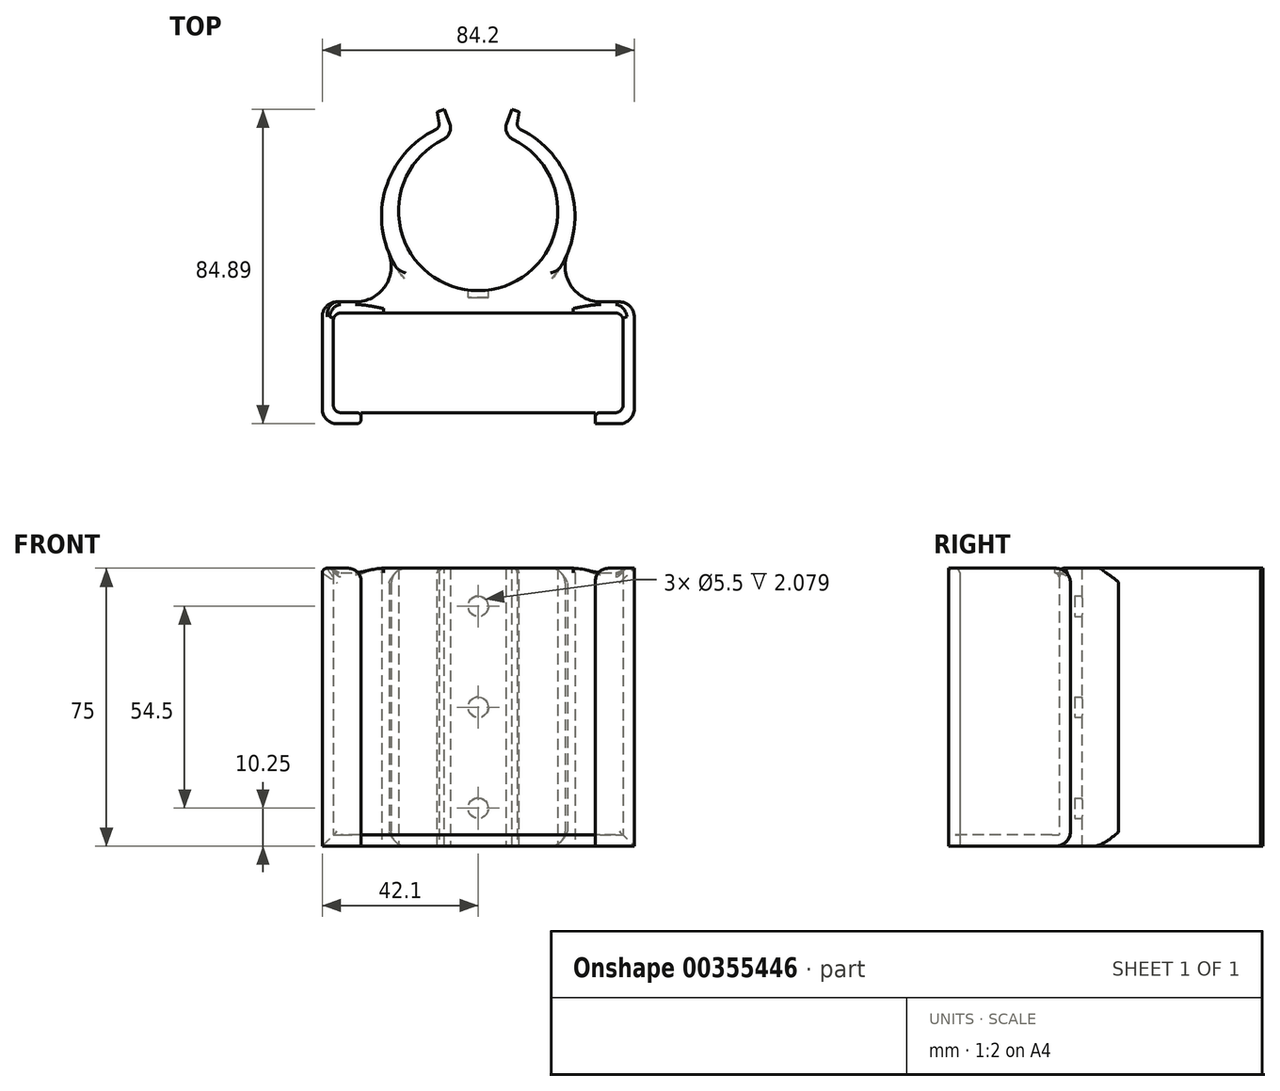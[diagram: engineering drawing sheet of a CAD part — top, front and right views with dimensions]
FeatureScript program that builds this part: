
annotation { "Feature Type Name" : "Feature", "Feature Type Description" : "" }
export const myFeature = defineFeature(function(context is Context, id is Id, definition is map)
    precondition{}
    {
        {
            var Q0;
            Q0=qCreatedBy(makeId("Top.planeOp"),FACE);
            var sketch = newSketch(context, id + "F0", { "sketchPlane" : qUnion([Q0])});
            skLineSegment(sketch, "E0", {"start": v(39.1, 0) * mm, "end": v(42.1, 0) * mm});
            skLineSegment(sketch, "E1", {"start": v(42.1, 0) * mm, "end": v(42.1, -3) * mm});
            skLineSegment(sketch, "E2", {"start": v(42.1, -3) * mm, "end": v(42.1, -29.9) * mm});
            skLineSegment(sketch, "E3", {"start": v(42.1, -29.9) * mm, "end": v(42.1, -32.9) * mm});
            skLineSegment(sketch, "E4", {"start": v(42.1, -32.9) * mm, "end": v(33.1, -32.9) * mm});
            skLineSegment(sketch, "E5", {"start": v(33.1, -29.9) * mm, "end": v(39.1, -29.9) * mm});
            skLineSegment(sketch, "E6", {"start": v(39.1, -29.9) * mm, "end": v(39.1, -3) * mm});
            skLineSegment(sketch, "E7", {"start": v(39.1, -3) * mm, "end": v(-39.1, -3) * mm});
            skLineSegment(sketch, "E8", {"start": v(-39.1, -3) * mm, "end": v(-39.1, -29.9) * mm});
            skLineSegment(sketch, "E9", {"start": v(-39.1, -29.9) * mm, "end": v(-33.1, -29.9) * mm});
            skLineSegment(sketch, "E10", {"start": v(-33.1, -32.9) * mm, "end": v(-42.1, -32.9) * mm});
            skLineSegment(sketch, "E11", {"start": v(-42.1, -32.9) * mm, "end": v(-42.1, 0) * mm});
            skLineSegment(sketch, "E12", {"start": v(-42.1, 0) * mm, "end": v(-33.1, 0) * mm});
            skArc(sketch, "E13", {"start": v(-33.1, 0) * mm, "mid": v(-25.18, 4.14) * mm, "end": v(-24.06, 13) * mm});
            skArc(sketch, "E14", {"start": v(24.06, 13) * mm, "mid": v(25.18, 4.14) * mm, "end": v(33.1, 0) * mm});
            skArc(sketch, "E15", {"start": v(-15.28, 44.25) * mm, "mid": v(-25.12, 30.16) * mm, "end": v(-24.06, 13) * mm});
            skArc(sketch, "E16", {"start": v(24.06, 13) * mm, "mid": v(25.12, 30.16) * mm, "end": v(15.28, 44.25) * mm});
            skLineSegment(sketch, "E17", {"start": v(33.1, 0) * mm, "end": v(39.1, 0) * mm});
            skLineSegment(sketch, "E18", {"start": v(-33.1, -32.9) * mm, "end": v(33.1, -32.9) * mm});
            skLineSegment(sketch, "E19", {"start": v(-33.1, -29.9) * mm, "end": v(33.1, -29.9) * mm});
            skLineSegment(sketch, "E20", {"start": v(-33.1, 0) * mm, "end": v(33.1, 0) * mm});
            skLineSegment(sketch, "E21", {"start": v(-42.1, -32.9) * mm, "end": v(-31.6, -32.9) * mm});
            skLineSegment(sketch, "E22", {"start": v(-31.6, -32.9) * mm, "end": v(-31.6, -29.9) * mm});
            skLineSegment(sketch, "E23", {"start": v(42.1, -32.9) * mm, "end": v(31.6, -32.9) * mm});
            skLineSegment(sketch, "E24", {"start": v(31.6, -32.9) * mm, "end": v(31.6, -29.9) * mm});
            skArc(sketch, "E25", {"start": v(-5.92, 45.2) * mm, "mid": v(0, 3.04) * mm, "end": v(5.9, 45.2) * mm});
            skLineSegment(sketch, "E26", {"start": v(5.9, 45.2) * mm, "end": v(9.5, 54.53) * mm});
            skLineSegment(sketch, "E27", {"start": v(-9.5, 54.53) * mm, "end": v(-5.92, 45.2) * mm});
            skLineSegment(sketch, "E28", {"start": v(9.5, 54.53) * mm, "end": v(11.36, 53.81) * mm});
            skLineSegment(sketch, "E29", {"start": v(-9.5, 54.53) * mm, "end": v(-11.37, 53.82) * mm});
            skLineSegment(sketch, "E30", {"start": v(-11.37, 53.82) * mm, "end": v(-10.43, 47.02) * mm});
            skPoint(sketch, "E30.endSnap0", {"position": v(-10.43, 54.17) * mm});
            skLineSegment(sketch, "E31", {"start": v(11.36, 53.81) * mm, "end": v(10.42, 47.02) * mm});
            skPoint(sketch, "E31.endSnap0", {"position": v(10.42, 54.17) * mm});
            skArc(sketch, "E32", {"start": v(-10.43, 47.02) * mm, "mid": v(-24.22, 32.8) * mm, "end": v(-24.06, 13) * mm});
            skArc(sketch, "E33", {"start": v(24.06, 13) * mm, "mid": v(24.22, 32.8) * mm, "end": v(10.42, 47.02) * mm});
            skSolve(sketch);
        }
        {
            var Q0;
            {var subQ1=sQuery(id+"F0.wireOp",EDGE,"E5");Q0=makeQuery(id+"F0.imprint","IMPRINT",FACE,{"disambiguationData":[TD([[makeQuery(id+"F0.imprint","IMPRINT",EDGE,{"derivedFrom":subQ1}),1.0]])]});}
            extrude(context, id + "F1", {"entities" : qUnion([Q0]), "depth" : 3 * mm});
        }
        {
            var Q0;
            Q0=makeQuery(id+"F0.imprint","IMPRINT",FACE,{"disambiguationData":[TD([[makeQuery(id+"F0.imprint","IMPRINT",EDGE,{"derivedFrom":sQuery(id+"F0.wireOp",EDGE,"E18")}),1.0]])]});
            extrude(context, id + "F2", {"entities" : qUnion([Q0]), "operationType" : NewBodyOperationType.ADD, "depth" : 8 * mm});
        }
        {
            var Q0;
            Q0=makeQuery(id+"F0.imprint","IMPRINT",FACE,{"disambiguationData":[TD([[makeQuery(id+"F0.imprint","IMPRINT",EDGE,{"derivedFrom":sQuery(id+"F0.wireOp",EDGE,"E0")}),-1.0]])]});
            var Q1;
            {var subQ1=sQuery(id+"F0.wireOp",EDGE,"E13");Q1=makeQuery(id+"F0.imprint","IMPRINT",FACE,{"disambiguationData":[TD([[makeQuery(id+"F0.imprint","IMPRINT",EDGE,{"derivedFrom":subQ1}),-1.0]])]});}
            extrude(context, id + "F3", {"entities" : qUnion([Q0, Q1]), "operationType" : NewBodyOperationType.ADD, "depth" : 75 * mm});
        }
        {
            var Q0;
            Q0=makeQuery(id+"F3.opExtrude","CAP_FACE",FACE,{"disambiguationData":[OSD([sQuery(id+"F0.wireOp",EDGE,"E0"),sQuery(id+"F0.wireOp",EDGE,"E1"),sQuery(id+"F0.wireOp",EDGE,"E2"),sQuery(id+"F0.wireOp",EDGE,"E3"),sQuery(id+"F0.wireOp",EDGE,"E5"),sQuery(id+"F0.wireOp",EDGE,"E6"),sQuery(id+"F0.wireOp",EDGE,"E7"),sQuery(id+"F0.wireOp",EDGE,"E8"),sQuery(id+"F0.wireOp",EDGE,"E9"),sQuery(id+"F0.wireOp",EDGE,"E11"),sQuery(id+"F0.wireOp",EDGE,"E12"),sQuery(id+"F0.wireOp",EDGE,"E13"),sQuery(id+"F0.wireOp",EDGE,"E14"),sQuery(id+"F0.wireOp",EDGE,"E17"),sQuery(id+"F0.wireOp",EDGE,"E19"),sQuery(id+"F0.wireOp",EDGE,"E21"),sQuery(id+"F0.wireOp",EDGE,"E22"),sQuery(id+"F0.wireOp",EDGE,"E23"),sQuery(id+"F0.wireOp",EDGE,"E24"),sQuery(id+"F0.wireOp",EDGE,"E25"),sQuery(id+"F0.wireOp",EDGE,"E26"),sQuery(id+"F0.wireOp",EDGE,"E27"),sQuery(id+"F0.wireOp",EDGE,"E28"),sQuery(id+"F0.wireOp",EDGE,"E29"),sQuery(id+"F0.wireOp",EDGE,"E30"),sQuery(id+"F0.wireOp",EDGE,"E31"),sQuery(id+"F0.wireOp",EDGE,"E32"),sQuery(id+"F0.wireOp",EDGE,"E33")])],"isStart":false});
            var sketch = newSketch(context, id + "F4", { "sketchPlane" : qUnion([Q0])});
            skLineSegment(sketch, "E34", {"start": v(0, 6.04) * mm, "end": v(10.94, 6.04) * mm});
            skLineSegment(sketch, "E35", {"start": v(10.94, 6.04) * mm, "end": v(-10.96, 6.04) * mm});
            skArc(sketch, "E36", {"start": v(-10.96, 6.04) * mm, "mid": v(0, 3.04) * mm, "end": v(10.94, 6.04) * mm});
            skSolve(sketch);
        }
        {
            var Q0;
            {var subQ0=sQuery(id+"F4.wireOp",EDGE,"E36");Q0=makeQuery(id+"F4.imprint","IMPRINT",FACE,{"disambiguationData":[TD([[makeQuery(id+"F4.imprint","IMPRINT",EDGE,{"derivedFrom":subQ0}),1.0]])]});}
            extrude(context, id + "F5", {"entities" : qUnion([Q0]), "operationType" : NewBodyOperationType.ADD, "oppositeDirection" : true, "depth" : 75 * mm});
        }
        {
            var Q0;
            Q0=makeQuery(id+"F5.opExtrude","SWEPT_FACE",FACE,{"disambiguationData":[OSD([sQuery(id+"F4.wireOp",EDGE,"E35")])]});
            var sketch = newSketch(context, id + "F6", { "sketchPlane" : qUnion([Q0])});
            skCircle(sketch, "E37", {"center": v(0, 10.25) * mm, "radius": 2.75 * mm});
            skCircle(sketch, "E38", {"center": v(0, 64.75) * mm, "radius": 2.75 * mm});
            skLineSegment(sketch, "E39", {"start": v(0, 75) * mm, "end": v(0, 37.5) * mm});
            skCircle(sketch, "E40", {"center": v(0, 37.5) * mm, "radius": 2.75 * mm});
            skSolve(sketch);
        }
        {
            var Q0;
            Q0=makeQuery(id+"F6.imprint","IMPRINT",FACE,{"disambiguationData":[TD([[makeQuery(id+"F6.imprint","IMPRINT",EDGE,{"derivedFrom":sQuery(id+"F6.wireOp",EDGE,"E38")}),1.0]])]});
            var Q1;
            Q1=makeQuery(id+"F6.imprint","IMPRINT",FACE,{"disambiguationData":[TD([[makeQuery(id+"F6.imprint","IMPRINT",EDGE,{"derivedFrom":sQuery(id+"F6.wireOp",EDGE,"E37")}),1.0]])]});
            var Q2;
            Q2=makeQuery(id+"F6.imprint","IMPRINT",FACE,{"disambiguationData":[TD([[makeQuery(id+"F6.imprint","IMPRINT",EDGE,{"derivedFrom":sQuery(id+"F6.wireOp",EDGE,"E40")}),1.0]])]});
            extrude(context, id + "F7", {"entities" : qUnion([Q0, Q1, Q2]), "operationType" : NewBodyOperationType.REMOVE, "oppositeDirection" : true, "depth" : 4.9 * mm});
        }
        {
            var Q0;
            {var subQ0=sQuery(id+"F4.wireOp",EDGE,"E36");Q0=makeQuery(id+"F4.imprint","IMPRINT",FACE,{"disambiguationData":[TD([[makeQuery(id+"F4.imprint","IMPRINT",EDGE,{"derivedFrom":subQ0}),1.0]])]});}
            extrude(context, id + "F8", {"entities" : qUnion([Q0]), "operationType" : NewBodyOperationType.REMOVE, "oppositeDirection" : true, "depth" : 75 * mm});
        }
        {
            var Q0;
            Q0=makeQuery(id+"F5.boolean.opBoolean","MERGE",FACE,{"derivedFrom":[makeQuery(id+"F3.opExtrude","CAP_FACE",FACE,{"disambiguationData":[OSD([sQuery(id+"F0.wireOp",EDGE,"E0"),sQuery(id+"F0.wireOp",EDGE,"E1"),sQuery(id+"F0.wireOp",EDGE,"E2"),sQuery(id+"F0.wireOp",EDGE,"E3"),sQuery(id+"F0.wireOp",EDGE,"E5"),sQuery(id+"F0.wireOp",EDGE,"E6"),sQuery(id+"F0.wireOp",EDGE,"E7"),sQuery(id+"F0.wireOp",EDGE,"E8"),sQuery(id+"F0.wireOp",EDGE,"E9"),sQuery(id+"F0.wireOp",EDGE,"E11"),sQuery(id+"F0.wireOp",EDGE,"E12"),sQuery(id+"F0.wireOp",EDGE,"E13"),sQuery(id+"F0.wireOp",EDGE,"E14"),sQuery(id+"F0.wireOp",EDGE,"E17"),sQuery(id+"F0.wireOp",EDGE,"E19"),sQuery(id+"F0.wireOp",EDGE,"E21"),sQuery(id+"F0.wireOp",EDGE,"E22"),sQuery(id+"F0.wireOp",EDGE,"E23"),sQuery(id+"F0.wireOp",EDGE,"E24"),sQuery(id+"F0.wireOp",EDGE,"E25"),sQuery(id+"F0.wireOp",EDGE,"E26"),sQuery(id+"F0.wireOp",EDGE,"E27"),sQuery(id+"F0.wireOp",EDGE,"E28"),sQuery(id+"F0.wireOp",EDGE,"E29"),sQuery(id+"F0.wireOp",EDGE,"E30"),sQuery(id+"F0.wireOp",EDGE,"E31"),sQuery(id+"F0.wireOp",EDGE,"E32"),sQuery(id+"F0.wireOp",EDGE,"E33")])],"isStart":false}),makeQuery(id+"F5.opExtrude","CAP_FACE",FACE,{"disambiguationData":[OSD([sQuery(id+"F4.wireOp",EDGE,"E35"),sQuery(id+"F4.wireOp",EDGE,"E36")])],"isStart":true})]});
            var sketch = newSketch(context, id + "F9", { "sketchPlane" : qUnion([Q0])});
            skLineSegment(sketch, "E41", {"start": v(-9.5, 54.53) * mm, "end": v(-8.6, 52.2) * mm});
            skLineSegment(sketch, "E42", {"start": v(-8.6, 52.2) * mm, "end": v(-11.02, 51.27) * mm});
            skLineSegment(sketch, "E43", {"start": v(9.5, 54.53) * mm, "end": v(8.6, 52.2) * mm});
            skLineSegment(sketch, "E44", {"start": v(8.6, 52.2) * mm, "end": v(11, 51.27) * mm});
            skSolve(sketch);
        }
        {
            var Q0;
            Q0 = qSketchRegion(id + "F9", true);
            var Q1;
            Q1=makeQuery(id+"F9.imprint","IMPRINT",FACE,{"disambiguationData":[TD([[makeQuery(id+"F9.imprint","IMPRINT",EDGE,{"derivedFrom":sQuery(id+"F9.wireOp",EDGE,"E43")}),-1.0]])]});
            var Q2;
            Q2=makeQuery(id+"F9.imprint","IMPRINT",FACE,{"disambiguationData":[TD([[makeQuery(id+"F9.imprint","IMPRINT",EDGE,{"derivedFrom":sQuery(id+"F9.wireOp",EDGE,"E41")}),-1.0]])]});
            extrude(context, id + "F10", {"entities" : qUnion([Q0, Q1, Q2]), "operationType" : NewBodyOperationType.REMOVE, "oppositeDirection" : true, "depth" : 75 * mm});
        }
        {
            var Q0;
            Q0=makeQuery(id+"F3.opExtrude","SWEPT_FACE",FACE,{"disambiguationData":[OSD([sQuery(id+"F0.wireOp",EDGE,"E26")])]});
            extrude(context, id + "F11", {"entities" : qUnion([Q0]), "operationType" : NewBodyOperationType.REMOVE, "oppositeDirection" : true, "depth" : .584 * mm});
        }
        {
            var Q0;
            Q0=makeQuery(id+"F3.opExtrude","SWEPT_FACE",FACE,{"disambiguationData":[OSD([sQuery(id+"F0.wireOp",EDGE,"E27")])]});
            extrude(context, id + "F12", {"entities" : qUnion([Q0]), "operationType" : NewBodyOperationType.REMOVE, "oppositeDirection" : true, "depth" : .584 * mm});
        }
        {
            var Q0;
            Q0=makeQuery(id+"F3.opExtrude","SWEPT_EDGE",EDGE,{"disambiguationData":[OSD([sQuery(id+"F0.wireOp",EDGE,"E11"),sQuery(id+"F0.wireOp",EDGE,"E12")])]});
            var Q1;
            Q1=makeQuery(id+"F3.opExtrude","SWEPT_EDGE",EDGE,{"disambiguationData":[OSD([sQuery(id+"F0.wireOp",EDGE,"E11"),sQuery(id+"F0.wireOp",EDGE,"E21")])]});
            var Q2;
            Q2=makeQuery(id+"F3.opExtrude","SWEPT_EDGE",EDGE,{"disambiguationData":[OSD([sQuery(id+"F0.wireOp",EDGE,"E3"),sQuery(id+"F0.wireOp",EDGE,"E23")])]});
            var Q3;
            Q3=makeQuery(id+"F3.opExtrude","SWEPT_EDGE",EDGE,{"disambiguationData":[OSD([sQuery(id+"F0.wireOp",EDGE,"E0"),sQuery(id+"F0.wireOp",EDGE,"E1")])]});
            var Q4;
            Q4=makeQuery(id+"F3.opExtrude","CAP_EDGE",EDGE,{"disambiguationData":[OSD([sQuery(id+"F0.wireOp",EDGE,"E1"),sQuery(id+"F0.wireOp",EDGE,"E2"),sQuery(id+"F0.wireOp",EDGE,"E3")])],"isStart":true});
            var Q5;
            Q5=makeQuery(id+"F3.boolean.opBoolean","MERGE",EDGE,{"derivedFrom":[makeQuery(id+"F2.opExtrude","CAP_EDGE",EDGE,{"disambiguationData":[OSD([sQuery(id+"F0.wireOp",EDGE,"E18")])],"isStart":true}),makeQuery(id+"F3.opExtrude","CAP_EDGE",EDGE,{"disambiguationData":[OSD([sQuery(id+"F0.wireOp",EDGE,"E21")])],"isStart":true}),makeQuery(id+"F3.opExtrude","CAP_EDGE",EDGE,{"disambiguationData":[OSD([sQuery(id+"F0.wireOp",EDGE,"E23")])],"isStart":true})]});
            var Q6;
            Q6=makeQuery(id+"F3.opExtrude","CAP_EDGE",EDGE,{"disambiguationData":[OSD([sQuery(id+"F0.wireOp",EDGE,"E11")])],"isStart":true});
            var Q7;
            Q7=makeQuery(id+"F3.opExtrude","CAP_EDGE",EDGE,{"disambiguationData":[OSD([sQuery(id+"F0.wireOp",EDGE,"E13")])],"isStart":true});
            var Q8;
            Q8=makeQuery(id+"F3.opExtrude","CAP_EDGE",EDGE,{"disambiguationData":[OSD([sQuery(id+"F0.wireOp",EDGE,"E14")])],"isStart":true});
            var Q9;
            Q9=makeQuery(id+"F3.opExtrude","CAP_EDGE",EDGE,{"disambiguationData":[OSD([sQuery(id+"F0.wireOp",EDGE,"E14")])],"isStart":false});
            var Q10;
            Q10=makeQuery(id+"F3.opExtrude","CAP_EDGE",EDGE,{"disambiguationData":[OSD([sQuery(id+"F0.wireOp",EDGE,"E13")])],"isStart":false});
            fillet(context, id + "F13", {"entities" : qUnion([Q0, Q1, Q2, Q3, Q4, Q5, Q6, Q7, Q8, Q9, Q10]), "radius" : 4 * mm, "tangentPropagation" : true, "allowEdgeOverflow" : false});
        }
        {
            var Q0;
            Q0=makeQuery(id+"F3.opExtrude","SWEPT_EDGE",EDGE,{"disambiguationData":[OSD([sQuery(id+"F0.wireOp",EDGE,"E5"),sQuery(id+"F0.wireOp",EDGE,"E6")])]});
            var Q1;
            Q1=makeQuery(id+"F3.opExtrude","SWEPT_EDGE",EDGE,{"disambiguationData":[OSD([sQuery(id+"F0.wireOp",EDGE,"E6"),sQuery(id+"F0.wireOp",EDGE,"E7")])]});
            var Q2;
            Q2=makeQuery(id+"F3.opExtrude","SWEPT_EDGE",EDGE,{"disambiguationData":[OSD([sQuery(id+"F0.wireOp",EDGE,"E7"),sQuery(id+"F0.wireOp",EDGE,"E8")])]});
            var Q3;
            Q3=makeQuery(id+"F3.opExtrude","SWEPT_EDGE",EDGE,{"disambiguationData":[OSD([sQuery(id+"F0.wireOp",EDGE,"E8"),sQuery(id+"F0.wireOp",EDGE,"E9")])]});
            var Q4;
            {var subQ0=sQuery(id+"F0.wireOp",EDGE,"E19");var subQ1=sQuery(id+"F0.wireOp",EDGE,"E9");var subQ2=sQuery(id+"F0.wireOp",EDGE,"E8");var subQ3=sQuery(id+"F0.wireOp",EDGE,"E6");var subQ4=sQuery(id+"F0.wireOp",EDGE,"E5");var subQ5=makeQuery(id+"F1.opExtrude","CAP_FACE",FACE,{"disambiguationData":[OSD([subQ4,subQ3,sQuery(id+"F0.wireOp",EDGE,"E7"),subQ2,subQ1,subQ0])],"isStart":false});var subQ6=makeQuery(id+"F2.opExtrude","SWEPT_FACE",FACE,{"disambiguationData":[OSD([subQ0])]});var subQ7=makeQuery(id+"F1.opExtrude","CAP_EDGE",EDGE,{"disambiguationData":[OSD([subQ4,subQ1,subQ0])],"isStart":false});var subQ8=makeQuery(id+"F1.opExtrude","SWEPT_FACE",FACE,{"disambiguationData":[OSD([subQ4,subQ1,subQ0])]});Q4=makeQuery(id+"F3.boolean.opBoolean","MERGE",EDGE,{"derivedFrom":[makeQuery(id+"F2.boolean.opBoolean","SPLIT",EDGE,{"disambiguationData":[topologyDisambiguationEdgeConnected([subQ5,subQ8]),TD([makeQuery(id+"F1.opExtrude","SWEPT_FACE",FACE,{"disambiguationData":[OSD([subQ3])]})])],"derivedFrom":subQ7}),makeQuery(id+"F2.boolean.opBoolean","SPLIT",EDGE,{"disambiguationData":[topologyDisambiguationEdgeConnected([subQ5,subQ8]),TD([makeQuery(id+"F1.opExtrude","SWEPT_FACE",FACE,{"disambiguationData":[OSD([subQ2])]})])],"derivedFrom":subQ7}),makeQuery(id+"F2.boolean.opBoolean","SPLIT",EDGE,{"disambiguationData":[topologyDisambiguationEdgeConnected([subQ5,subQ6])],"derivedFrom":subQ7})]});}
            var Q5;
            Q5=makeQuery(id+"F1.opExtrude","CAP_EDGE",EDGE,{"disambiguationData":[OSD([sQuery(id+"F0.wireOp",EDGE,"E8")])],"isStart":false});
            var Q6;
            Q6=makeQuery(id+"F1.opExtrude","CAP_EDGE",EDGE,{"disambiguationData":[OSD([sQuery(id+"F0.wireOp",EDGE,"E7")])],"isStart":false});
            var Q7;
            Q7=makeQuery(id+"F1.opExtrude","CAP_EDGE",EDGE,{"disambiguationData":[OSD([sQuery(id+"F0.wireOp",EDGE,"E6")])],"isStart":false});
            fillet(context, id + "F14", {"entities" : qUnion([Q0, Q1, Q2, Q3, Q4, Q5, Q6, Q7]), "radius" : 2 * mm, "tangentPropagation" : true, "allowEdgeOverflow" : false});
        }
        {
            var Q0;
            Q0=makeQuery(id+"F3.opExtrude","CAP_EDGE",EDGE,{"disambiguationData":[OSD([sQuery(id+"F0.wireOp",EDGE,"E22")])],"isStart":false});
            var Q1;
            Q1=makeQuery(id+"F3.opExtrude","CAP_EDGE",EDGE,{"disambiguationData":[OSD([sQuery(id+"F0.wireOp",EDGE,"E24")])],"isStart":false});
            var Q2;
            Q2=makeQuery(id+"F2.opExtrude","CAP_EDGE",EDGE,{"disambiguationData":[OSD([sQuery(id+"F0.wireOp",EDGE,"E24")])],"isStart":false});
            var Q3;
            Q3=makeQuery(id+"F2.opExtrude","CAP_EDGE",EDGE,{"disambiguationData":[OSD([sQuery(id+"F0.wireOp",EDGE,"E22")])],"isStart":false});
            var Q4;
            Q4=makeQuery(id+"F10.boolean.opBoolean","COPY",EDGE,{"derivedFrom":makeQuery(id+"F10.opExtrude","CAP_EDGE",EDGE,{"disambiguationData":[OSD([sQuery(id+"F9.wireOp",EDGE,"E44")])],"isStart":false})});
            var Q5;
            Q5=makeQuery(id+"F10.boolean.opBoolean","COPY",EDGE,{"derivedFrom":makeQuery(id+"F10.opExtrude","CAP_EDGE",EDGE,{"disambiguationData":[OSD([sQuery(id+"F9.wireOp",EDGE,"E42")])],"isStart":false})});
            var Q6;
            Q6=makeQuery(id+"F10.boolean.opBoolean","COPY",EDGE,{"derivedFrom":makeQuery(id+"F10.opExtrude","CAP_EDGE",EDGE,{"disambiguationData":[OSD([sQuery(id+"F9.wireOp",EDGE,"E44")])],"isStart":true})});
            var Q7;
            Q7=makeQuery(id+"F10.boolean.opBoolean","COPY",EDGE,{"derivedFrom":makeQuery(id+"F10.opExtrude","CAP_EDGE",EDGE,{"disambiguationData":[OSD([sQuery(id+"F9.wireOp",EDGE,"E42")])],"isStart":true})});
            fillet(context, id + "F15", {"entities" : qUnion([Q0, Q1, Q2, Q3, Q4, Q5, Q6, Q7]), "radius" : 3.5 * mm, "tangentPropagation" : true, "allowEdgeOverflow" : false});
        }
        {
            var Q0;
            Q0=makeQuery(id+"F15.opFillet","BLEND_EDGE",EDGE,{"blendedFrom":[makeQuery(id+"F3.opExtrude","CAP_EDGE",EDGE,{"disambiguationData":[OSD([sQuery(id+"F0.wireOp",EDGE,"E22")])],"isStart":false}),makeQuery(id+"F3.boolean.opBoolean","MERGE",FACE,{"derivedFrom":[makeQuery(id+"F2.opExtrude","SWEPT_FACE",FACE,{"disambiguationData":[OSD([sQuery(id+"F0.wireOp",EDGE,"E18")])]}),makeQuery(id+"F3.opExtrude","SWEPT_FACE",FACE,{"disambiguationData":[OSD([sQuery(id+"F0.wireOp",EDGE,"E21")])]}),makeQuery(id+"F3.opExtrude","SWEPT_FACE",FACE,{"disambiguationData":[OSD([sQuery(id+"F0.wireOp",EDGE,"E23")])]})]})],"blendedInto":[makeQuery(id+"F3.boolean.opBoolean","MERGE",FACE,{"derivedFrom":[makeQuery(id+"F2.opExtrude","SWEPT_FACE",FACE,{"disambiguationData":[OSD([sQuery(id+"F0.wireOp",EDGE,"E18")])]}),makeQuery(id+"F3.opExtrude","SWEPT_FACE",FACE,{"disambiguationData":[OSD([sQuery(id+"F0.wireOp",EDGE,"E21")])]}),makeQuery(id+"F3.opExtrude","SWEPT_FACE",FACE,{"disambiguationData":[OSD([sQuery(id+"F0.wireOp",EDGE,"E23")])]})]})]});
            var Q1;
            {var subQ0=sQuery(id+"F0.wireOp",EDGE,"E19");Q1=makeQuery(id+"F15.opFillet","BLEND_EDGE",EDGE,{"blendedFrom":[makeQuery(id+"F3.opExtrude","CAP_EDGE",EDGE,{"disambiguationData":[OSD([sQuery(id+"F0.wireOp",EDGE,"E22")])],"isStart":false}),makeQuery(id+"F3.boolean.opBoolean","MERGE",FACE,{"derivedFrom":[makeQuery(id+"F2.opExtrude","SWEPT_FACE",FACE,{"disambiguationData":[OSD([subQ0])]}),makeQuery(id+"F3.opExtrude","SWEPT_FACE",FACE,{"disambiguationData":[OSD([sQuery(id+"F0.wireOp",EDGE,"E5"),subQ0])]}),makeQuery(id+"F3.opExtrude","SWEPT_FACE",FACE,{"disambiguationData":[OSD([sQuery(id+"F0.wireOp",EDGE,"E9"),subQ0])]})]})],"blendedInto":[makeQuery(id+"F3.boolean.opBoolean","MERGE",FACE,{"derivedFrom":[makeQuery(id+"F2.opExtrude","SWEPT_FACE",FACE,{"disambiguationData":[OSD([subQ0])]}),makeQuery(id+"F3.opExtrude","SWEPT_FACE",FACE,{"disambiguationData":[OSD([sQuery(id+"F0.wireOp",EDGE,"E5"),subQ0])]}),makeQuery(id+"F3.opExtrude","SWEPT_FACE",FACE,{"disambiguationData":[OSD([sQuery(id+"F0.wireOp",EDGE,"E9"),subQ0])]})]})]});}
            fillet(context, id + "F16", {"entities" : qUnion([Q0, Q1]), "radius" : 1.25 * mm, "tangentPropagation" : true, "allowEdgeOverflow" : false});
        }
        {
            var Q0;
            {var subQ0=sQuery(id+"F0.wireOp",EDGE,"E27");var subQ1=sQuery(id+"F4.wireOp",EDGE,"E36");var subQ8=sQuery(id+"F0.wireOp",EDGE,"E26");var subQ9=sQuery(id+"F0.wireOp",EDGE,"E25");var subQ37=makeQuery(id+"F3.opExtrude","SWEPT_FACE",FACE,{"disambiguationData":[OSD([subQ9])]});Q0=makeQuery(id+"F12.boolean.opBoolean","INTERSECT",EDGE,{"derivedFrom":[makeQuery(id+"F8.boolean.opBoolean","MERGE",FACE,{"derivedFrom":[makeQuery(id+"F5.boolean.opBoolean","SPLIT",FACE,{"disambiguationData":[TD([makeQuery(id+"F3.opExtrude","SWEPT_FACE",FACE,{"disambiguationData":[OSD([subQ0])]})])],"derivedFrom":subQ37}),makeQuery(id+"F5.boolean.opBoolean","SPLIT",FACE,{"disambiguationData":[TD([makeQuery(id+"F3.opExtrude","SWEPT_FACE",FACE,{"disambiguationData":[OSD([subQ8])]})])],"derivedFrom":subQ37}),makeQuery(id+"F8.opExtrude","SWEPT_FACE",FACE,{"disambiguationData":[OSD([subQ1])]})]}),makeQuery(id+"F12.opExtrude","CAP_FACE",FACE,{"disambiguationData":[OSD([subQ0])],"isStart":false})]});}
            var Q1;
            {var subQ0=sQuery(id+"F0.wireOp",EDGE,"E26");var subQ1=sQuery(id+"F4.wireOp",EDGE,"E36");var subQ8=sQuery(id+"F0.wireOp",EDGE,"E27");var subQ9=sQuery(id+"F0.wireOp",EDGE,"E25");var subQ37=makeQuery(id+"F3.opExtrude","SWEPT_FACE",FACE,{"disambiguationData":[OSD([subQ9])]});Q1=makeQuery(id+"F11.boolean.opBoolean","INTERSECT",EDGE,{"derivedFrom":[makeQuery(id+"F8.boolean.opBoolean","MERGE",FACE,{"derivedFrom":[makeQuery(id+"F5.boolean.opBoolean","SPLIT",FACE,{"disambiguationData":[TD([makeQuery(id+"F3.opExtrude","SWEPT_FACE",FACE,{"disambiguationData":[OSD([subQ8])]})])],"derivedFrom":subQ37}),makeQuery(id+"F5.boolean.opBoolean","SPLIT",FACE,{"disambiguationData":[TD([makeQuery(id+"F3.opExtrude","SWEPT_FACE",FACE,{"disambiguationData":[OSD([subQ0])]})])],"derivedFrom":subQ37}),makeQuery(id+"F8.opExtrude","SWEPT_FACE",FACE,{"disambiguationData":[OSD([subQ1])]})]}),makeQuery(id+"F11.opExtrude","CAP_FACE",FACE,{"disambiguationData":[OSD([subQ0])],"isStart":false})]});}
            fillet(context, id + "F17", {"entities" : qUnion([Q0, Q1]), "radius" : 3.5 * mm, "tangentPropagation" : true, "allowEdgeOverflow" : false});
        }
        {
            var Q0;
            Q0=makeQuery(id+"F3.opExtrude","SWEPT_EDGE",EDGE,{"disambiguationData":[OSD([sQuery(id+"F0.wireOp",EDGE,"E30"),sQuery(id+"F0.wireOp",EDGE,"E32")])]});
            var Q1;
            Q1=makeQuery(id+"F3.opExtrude","SWEPT_EDGE",EDGE,{"disambiguationData":[OSD([sQuery(id+"F0.wireOp",EDGE,"E31"),sQuery(id+"F0.wireOp",EDGE,"E33")])]});
            fillet(context, id + "F18", {"entities" : qUnion([Q0, Q1]), "radius" : 1.5 * mm, "tangentPropagation" : true, "allowEdgeOverflow" : false});
        }
        {
            var Q0;
            Q0=makeQuery(id+"F3.opExtrude","CAP_EDGE",EDGE,{"disambiguationData":[OSD([sQuery(id+"F0.wireOp",EDGE,"E33")])],"isStart":false});
            var Q1;
            Q1=makeQuery(id+"F3.opExtrude","CAP_EDGE",EDGE,{"disambiguationData":[OSD([sQuery(id+"F0.wireOp",EDGE,"E32")])],"isStart":false});
            var Q2;
            {var subQ0=sQuery(id+"F4.wireOp",EDGE,"E36");var subQ3=sQuery(id+"F0.wireOp",EDGE,"E26");var subQ4=sQuery(id+"F0.wireOp",EDGE,"E25");var subQ7=sQuery(id+"F0.wireOp",EDGE,"E27");var subQ9=makeQuery(id+"F3.opExtrude","CAP_EDGE",EDGE,{"disambiguationData":[OSD([subQ4])],"isStart":false});Q2=makeQuery(id+"F8.boolean.opBoolean","MERGE",EDGE,{"derivedFrom":[makeQuery(id+"F5.boolean.opBoolean","SPLIT",EDGE,{"disambiguationData":[TD([makeQuery(id+"F3.opExtrude","SWEPT_FACE",FACE,{"disambiguationData":[OSD([subQ7])]})])],"derivedFrom":subQ9}),makeQuery(id+"F5.boolean.opBoolean","SPLIT",EDGE,{"disambiguationData":[TD([makeQuery(id+"F3.opExtrude","SWEPT_FACE",FACE,{"disambiguationData":[OSD([subQ3])]})])],"derivedFrom":subQ9}),makeQuery(id+"F8.opExtrude","CAP_EDGE",EDGE,{"disambiguationData":[OSD([subQ0])],"isStart":true})]});}
            fillet(context, id + "F19", {"entities" : qUnion([Q0, Q1, Q2]), "radius" : 1.25 * mm, "tangentPropagation" : true, "allowEdgeOverflow" : false});
        }
    });
